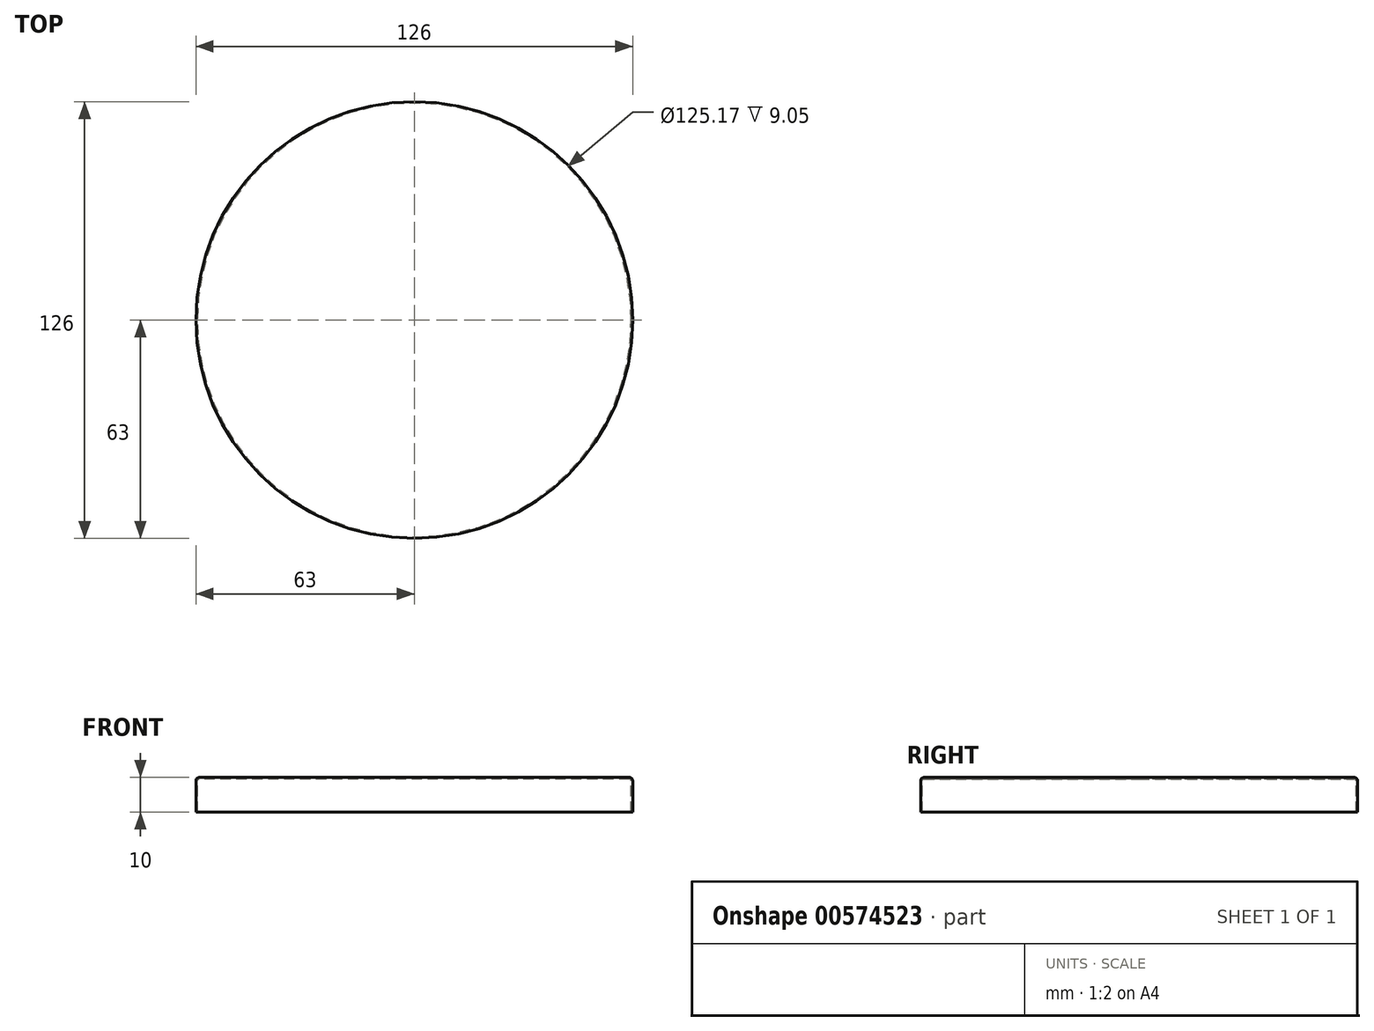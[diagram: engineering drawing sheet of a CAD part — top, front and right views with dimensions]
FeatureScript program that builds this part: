
annotation { "Feature Type Name" : "Feature", "Feature Type Description" : "" }
export const myFeature = defineFeature(function(context is Context, id is Id, definition is map)
    precondition{}
    {
        {
            var Q0;
            Q0=qCreatedBy(makeId("Front.planeOp"),FACE);
            var sketch = newSketch(context, id + "F0", { "sketchPlane" : qUnion([Q0])});
            skLineSegment(sketch, "E0.bottom", {"start": v(0, 0) * mm, "end": v(62.05, 0) * mm});
            skLineSegment(sketch, "E0.top", {"start": v(0, -0.41) * mm, "end": v(62.05, -0.41) * mm});
            skLineSegment(sketch, "E0.left", {"start": v(0, 0) * mm, "end": v(0, -0.41) * mm});
            skLineSegment(sketch, "E1.top", {"start": v(63, -10) * mm, "end": v(62.59, -10) * mm});
            skLineSegment(sketch, "E1.left", {"start": v(63, -0.95) * mm, "end": v(63, -10) * mm});
            skLineSegment(sketch, "E1.right", {"start": v(62.59, -0.95) * mm, "end": v(62.59, -10) * mm});
            skPoint(sketch, "E2.visualSharp", {"position": v(62.59, -0.41) * mm});
            skArc(sketch, "E2.filletArc", {"start": v(62.59, -0.95) * mm, "mid": v(62.43, -0.57) * mm, "end": v(62.05, -0.41) * mm});
            skArc(sketch, "E3.filletArc", {"start": v(63, -0.95) * mm, "mid": v(62.72, -0.28) * mm, "end": v(62.05, 0) * mm});
            skSolve(sketch);
        }
        {
            var Q0;
            Q0=makeQuery(id+"F0.imprint","IMPRINT",FACE,{"disambiguationData":[TD([[makeQuery(id+"F0.imprint","IMPRINT",EDGE,{"derivedFrom":sQuery(id+"F0.wireOp",EDGE,"E0.bottom")}),-1.0]])]});
            var Q1;
            Q1=sQuery(id+"F0.wireOp",EDGE,"E0.left");
            revolve(context, id + "F1", {"entities" : qUnion([Q0]), "axis" : qUnion([Q1]), "revolveType" : RevolveType.FULL});
        }
    });
